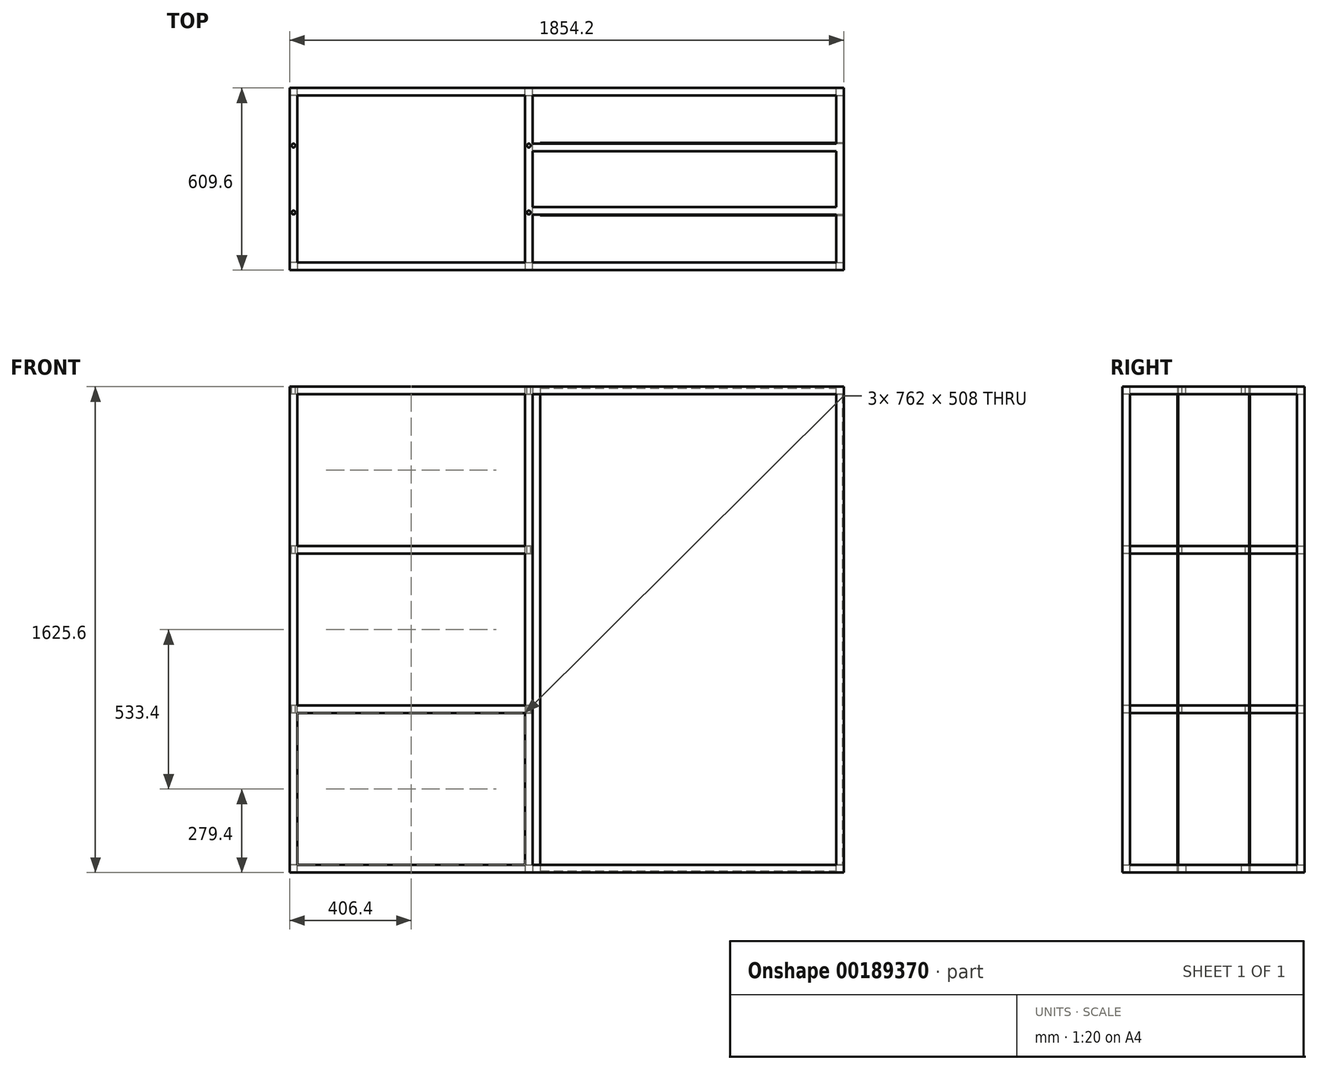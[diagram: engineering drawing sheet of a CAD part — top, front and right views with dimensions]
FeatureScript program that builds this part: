
annotation { "Feature Type Name" : "Feature", "Feature Type Description" : "" }
export const myFeature = defineFeature(function(context is Context, id is Id, definition is map)
    precondition{}
    {
        {
            var Q0;
            Q0=qCreatedBy(makeId("Front.planeOp"),FACE);
            var sketch = newSketch(context, id + "F0", { "sketchPlane" : qUnion([Q0])});
            skLineSegment(sketch, "E0.bottom", {"start": v(0, 0) * mm, "end": v(25.4, 0) * mm});
            skLineSegment(sketch, "E0.top", {"start": v(0, 25.4) * mm, "end": v(25.4, 25.4) * mm});
            skLineSegment(sketch, "E0.left", {"start": v(0, 0) * mm, "end": v(0, 25.4) * mm});
            skLineSegment(sketch, "E0.right", {"start": v(25.4, 0) * mm, "end": v(25.4, 25.4) * mm});
            skLineSegment(sketch, "E1.bottom", {"start": v(0, 533.4) * mm, "end": v(25.4, 533.4) * mm});
            skLineSegment(sketch, "E1.top", {"start": v(0, 558.8) * mm, "end": v(25.4, 558.8) * mm});
            skLineSegment(sketch, "E1.left", {"start": v(0, 533.4) * mm, "end": v(0, 558.8) * mm});
            skLineSegment(sketch, "E1.right", {"start": v(25.4, 533.4) * mm, "end": v(25.4, 558.8) * mm});
            skLineSegment(sketch, "E2.bottom", {"start": v(0, 1066.8) * mm, "end": v(25.4, 1066.8) * mm});
            skLineSegment(sketch, "E2.top", {"start": v(0, 1092.2) * mm, "end": v(25.4, 1092.2) * mm});
            skLineSegment(sketch, "E2.left", {"start": v(0, 1066.8) * mm, "end": v(0, 1092.2) * mm});
            skLineSegment(sketch, "E2.right", {"start": v(25.4, 1066.8) * mm, "end": v(25.4, 1092.2) * mm});
            skLineSegment(sketch, "E3.bottom", {"start": v(0, 1600.2) * mm, "end": v(25.4, 1600.2) * mm});
            skLineSegment(sketch, "E3.top", {"start": v(0, 1625.6) * mm, "end": v(25.4, 1625.6) * mm});
            skLineSegment(sketch, "E3.left", {"start": v(0, 1600.2) * mm, "end": v(0, 1625.6) * mm});
            skLineSegment(sketch, "E3.right", {"start": v(25.4, 1600.2) * mm, "end": v(25.4, 1625.6) * mm});
            skLineSegment(sketch, "E4", {"start": v(0, 25.4) * mm, "end": v(0, 558.8) * mm, "construction": true});
            skLineSegment(sketch, "E5", {"start": v(0, 558.8) * mm, "end": v(0, 1092.2) * mm, "construction": true});
            skLineSegment(sketch, "E6", {"start": v(0, 1092.2) * mm, "end": v(0, 1625.6) * mm, "construction": true});
            skLineSegment(sketch, "E7.bottom", {"start": v(787.4, 1625.6) * mm, "end": v(812.8, 1625.6) * mm});
            skLineSegment(sketch, "E7.top", {"start": v(787.4, 1600.2) * mm, "end": v(812.8, 1600.2) * mm});
            skLineSegment(sketch, "E7.left", {"start": v(787.4, 1625.6) * mm, "end": v(787.4, 1600.2) * mm});
            skLineSegment(sketch, "E7.right", {"start": v(812.8, 1625.6) * mm, "end": v(812.8, 1600.2) * mm});
            skLineSegment(sketch, "E8.bottom", {"start": v(787.4, 1092.2) * mm, "end": v(812.8, 1092.2) * mm});
            skLineSegment(sketch, "E8.top", {"start": v(787.4, 1066.8) * mm, "end": v(812.8, 1066.8) * mm});
            skLineSegment(sketch, "E8.left", {"start": v(787.4, 1092.2) * mm, "end": v(787.4, 1066.8) * mm});
            skLineSegment(sketch, "E8.right", {"start": v(812.8, 1092.2) * mm, "end": v(812.8, 1066.8) * mm});
            skLineSegment(sketch, "E9.bottom", {"start": v(787.4, 558.8) * mm, "end": v(812.8, 558.8) * mm});
            skLineSegment(sketch, "E9.top", {"start": v(787.4, 533.4) * mm, "end": v(812.8, 533.4) * mm});
            skLineSegment(sketch, "E9.left", {"start": v(787.4, 558.8) * mm, "end": v(787.4, 533.4) * mm});
            skLineSegment(sketch, "E9.right", {"start": v(812.8, 558.8) * mm, "end": v(812.8, 533.4) * mm});
            skLineSegment(sketch, "E10.bottom", {"start": v(787.4, 25.4) * mm, "end": v(812.8, 25.4) * mm});
            skLineSegment(sketch, "E10.top", {"start": v(787.4, 0) * mm, "end": v(812.8, 0) * mm});
            skLineSegment(sketch, "E10.left", {"start": v(787.4, 25.4) * mm, "end": v(787.4, 0) * mm});
            skLineSegment(sketch, "E10.right", {"start": v(812.8, 25.4) * mm, "end": v(812.8, 0) * mm});
            skLineSegment(sketch, "E11.bottom", {"start": v(1854.2, 1625.6) * mm, "end": v(1828.8, 1625.6) * mm});
            skLineSegment(sketch, "E11.top", {"start": v(1854.2, 1600.2) * mm, "end": v(1828.8, 1600.2) * mm});
            skLineSegment(sketch, "E11.left", {"start": v(1854.2, 1625.6) * mm, "end": v(1854.2, 1600.2) * mm});
            skLineSegment(sketch, "E11.right", {"start": v(1828.8, 1625.6) * mm, "end": v(1828.8, 1600.2) * mm});
            skLineSegment(sketch, "E12.bottom", {"start": v(1854.2, 0) * mm, "end": v(1828.8, 0) * mm});
            skLineSegment(sketch, "E12.top", {"start": v(1854.2, 25.4) * mm, "end": v(1828.8, 25.4) * mm});
            skLineSegment(sketch, "E12.left", {"start": v(1854.2, 0) * mm, "end": v(1854.2, 25.4) * mm});
            skLineSegment(sketch, "E12.right", {"start": v(1828.8, 0) * mm, "end": v(1828.8, 25.4) * mm});
            skSolve(sketch);
        }
        {
            var Q0;
            Q0 = qSketchRegion(id + "F0", true);
            extrude(context, id + "F1", {"entities" : qUnion([Q0]), "depth" : 609.6 * mm});
        }
        {
            var Q0;
            Q0=qCreatedBy(makeId("Right.planeOp"),FACE);
            var sketch = newSketch(context, id + "F2", { "sketchPlane" : qUnion([Q0])});
            skLineSegment(sketch, "E13.bottom", {"start": v(-609.6, 1600.2) * mm, "end": v(-584.2, 1600.2) * mm});
            skLineSegment(sketch, "E13.top", {"start": v(-609.6, 1625.6) * mm, "end": v(-584.2, 1625.6) * mm});
            skLineSegment(sketch, "E13.left", {"start": v(-609.6, 1625.6) * mm, "end": v(-609.6, 1600.2) * mm});
            skLineSegment(sketch, "E13.right", {"start": v(-584.2, 1625.6) * mm, "end": v(-584.2, 1600.2) * mm});
            skLineSegment(sketch, "E14.bottom", {"start": v(0, 1600.2) * mm, "end": v(-25.4, 1600.2) * mm});
            skLineSegment(sketch, "E14.top", {"start": v(0, 1625.6) * mm, "end": v(-25.4, 1625.6) * mm});
            skLineSegment(sketch, "E14.left", {"start": v(-25.4, 1625.6) * mm, "end": v(-25.4, 1600.2) * mm});
            skLineSegment(sketch, "E14.right", {"start": v(0, 1625.6) * mm, "end": v(0, 1600.2) * mm});
            skLineSegment(sketch, "E15.bottom", {"start": v(-609.6, 0) * mm, "end": v(-584.2, 0) * mm});
            skLineSegment(sketch, "E15.top", {"start": v(-609.6, 25.4) * mm, "end": v(-584.2, 25.4) * mm});
            skLineSegment(sketch, "E15.left", {"start": v(-609.6, 0) * mm, "end": v(-609.6, 25.4) * mm});
            skLineSegment(sketch, "E15.right", {"start": v(-584.2, 0) * mm, "end": v(-584.2, 25.4) * mm});
            skLineSegment(sketch, "E16.bottom", {"start": v(0, 0) * mm, "end": v(-25.4, 0) * mm});
            skLineSegment(sketch, "E16.top", {"start": v(0, 25.4) * mm, "end": v(-25.4, 25.4) * mm});
            skLineSegment(sketch, "E16.left", {"start": v(-25.4, 0) * mm, "end": v(-25.4, 25.4) * mm});
            skLineSegment(sketch, "E16.right", {"start": v(0, 0) * mm, "end": v(0, 25.4) * mm});
            skSolve(sketch);
        }
        {
            var Q0;
            Q0 = qSketchRegion(id + "F2", true);
            var Q1;
            Q1=makeQuery(id+"F1.opExtrude","SWEPT_FACE",FACE,{"disambiguationData":[OSD([sQuery(id+"F0.wireOp",EDGE,"E11.left")])]});
            extrude(context, id + "F3", {"entities" : qUnion([Q0]), "operationType" : NewBodyOperationType.ADD, "endBound" : BoundingType.UP_TO_SURFACE, "endBoundEntityFace" : qUnion([Q1]), "depth" : 25.4 * mm});
        }
        {
            var Q0;
            Q0=qCreatedBy(makeId("Right.planeOp"),FACE);
            var sketch = newSketch(context, id + "F4", { "sketchPlane" : qUnion([Q0])});
            skLineSegment(sketch, "E17.bottom", {"start": v(-609.6, 533.4) * mm, "end": v(-584.2, 533.4) * mm});
            skLineSegment(sketch, "E17.top", {"start": v(-609.6, 558.8) * mm, "end": v(-584.2, 558.8) * mm});
            skLineSegment(sketch, "E17.left", {"start": v(-609.6, 533.4) * mm, "end": v(-609.6, 558.8) * mm});
            skLineSegment(sketch, "E17.right", {"start": v(-584.2, 533.4) * mm, "end": v(-584.2, 558.8) * mm});
            skLineSegment(sketch, "E18.bottom", {"start": v(0, 533.4) * mm, "end": v(-25.4, 533.4) * mm});
            skLineSegment(sketch, "E18.top", {"start": v(0, 558.8) * mm, "end": v(-25.4, 558.8) * mm});
            skLineSegment(sketch, "E18.left", {"start": v(0, 533.4) * mm, "end": v(0, 558.8) * mm});
            skLineSegment(sketch, "E18.right", {"start": v(-25.4, 533.4) * mm, "end": v(-25.4, 558.8) * mm});
            skLineSegment(sketch, "E19.bottom", {"start": v(-609.6, 1092.2) * mm, "end": v(-584.2, 1092.2) * mm});
            skLineSegment(sketch, "E19.top", {"start": v(-609.6, 1066.8) * mm, "end": v(-584.2, 1066.8) * mm});
            skLineSegment(sketch, "E19.left", {"start": v(-609.6, 1092.2) * mm, "end": v(-609.6, 1066.8) * mm});
            skLineSegment(sketch, "E19.right", {"start": v(-584.2, 1092.2) * mm, "end": v(-584.2, 1066.8) * mm});
            skLineSegment(sketch, "E20.bottom", {"start": v(0, 1092.2) * mm, "end": v(-25.4, 1092.2) * mm});
            skLineSegment(sketch, "E20.top", {"start": v(0, 1066.8) * mm, "end": v(-25.4, 1066.8) * mm});
            skLineSegment(sketch, "E20.left", {"start": v(0, 1092.2) * mm, "end": v(0, 1066.8) * mm});
            skLineSegment(sketch, "E20.right", {"start": v(-25.4, 1092.2) * mm, "end": v(-25.4, 1066.8) * mm});
            skSolve(sketch);
        }
        {
            var Q0;
            Q0 = qSketchRegion(id + "F4", true);
            var Q1;
            Q1=makeQuery(id+"F1.opExtrude","SWEPT_FACE",FACE,{"disambiguationData":[OSD([sQuery(id+"F0.wireOp",EDGE,"E8.right")])]});
            extrude(context, id + "F5", {"entities" : qUnion([Q0]), "operationType" : NewBodyOperationType.ADD, "endBound" : BoundingType.UP_TO_SURFACE, "endBoundEntityFace" : qUnion([Q1]), "depth" : 25.4 * mm});
        }
        {
            var Q0;
            Q0=qCreatedBy(makeId("Top.planeOp"),FACE);
            var sketch = newSketch(context, id + "F6", { "sketchPlane" : qUnion([Q0])});
            skLineSegment(sketch, "E21.bottom", {"start": v(0, 0) * mm, "end": v(25.4, 0) * mm});
            skLineSegment(sketch, "E21.top", {"start": v(0, -25.4) * mm, "end": v(25.4, -25.4) * mm});
            skLineSegment(sketch, "E21.left", {"start": v(0, 0) * mm, "end": v(0, -25.4) * mm});
            skLineSegment(sketch, "E21.right", {"start": v(25.4, 0) * mm, "end": v(25.4, -25.4) * mm});
            skLineSegment(sketch, "E22.bottom", {"start": v(812.8, 0) * mm, "end": v(787.4, 0) * mm});
            skLineSegment(sketch, "E22.top", {"start": v(812.8, -25.4) * mm, "end": v(787.4, -25.4) * mm});
            skLineSegment(sketch, "E22.left", {"start": v(812.8, 0) * mm, "end": v(812.8, -25.4) * mm});
            skLineSegment(sketch, "E22.right", {"start": v(787.4, 0) * mm, "end": v(787.4, -25.4) * mm});
            skLineSegment(sketch, "E23.bottom", {"start": v(0, -609.6) * mm, "end": v(25.4, -609.6) * mm});
            skLineSegment(sketch, "E23.top", {"start": v(0, -584.2) * mm, "end": v(25.4, -584.2) * mm});
            skLineSegment(sketch, "E23.left", {"start": v(0, -609.6) * mm, "end": v(0, -584.2) * mm});
            skLineSegment(sketch, "E23.right", {"start": v(25.4, -609.6) * mm, "end": v(25.4, -584.2) * mm});
            skLineSegment(sketch, "E24.bottom", {"start": v(812.8, -609.6) * mm, "end": v(787.4, -609.6) * mm});
            skLineSegment(sketch, "E24.top", {"start": v(812.8, -584.2) * mm, "end": v(787.4, -584.2) * mm});
            skLineSegment(sketch, "E24.left", {"start": v(812.8, -609.6) * mm, "end": v(812.8, -584.2) * mm});
            skLineSegment(sketch, "E24.right", {"start": v(787.4, -609.6) * mm, "end": v(787.4, -584.2) * mm});
            skPoint(sketch, "E25.firstSnap0", {"position": v(800.1, -584.2) * mm});
            skLineSegment(sketch, "E25.bottom", {"start": v(1854.2, -584.2) * mm, "end": v(1828.8, -584.2) * mm});
            skLineSegment(sketch, "E25.top", {"start": v(1854.2, -609.6) * mm, "end": v(1828.8, -609.6) * mm});
            skLineSegment(sketch, "E25.left", {"start": v(1854.2, -584.2) * mm, "end": v(1854.2, -609.6) * mm});
            skLineSegment(sketch, "E25.right", {"start": v(1828.8, -584.2) * mm, "end": v(1828.8, -609.6) * mm});
            skLineSegment(sketch, "E26.bottom", {"start": v(1854.2, 0) * mm, "end": v(1828.8, 0) * mm});
            skLineSegment(sketch, "E26.top", {"start": v(1854.2, -25.4) * mm, "end": v(1828.8, -25.4) * mm});
            skLineSegment(sketch, "E26.left", {"start": v(1854.2, 0) * mm, "end": v(1854.2, -25.4) * mm});
            skLineSegment(sketch, "E26.right", {"start": v(1828.8, 0) * mm, "end": v(1828.8, -25.4) * mm});
            skSolve(sketch);
        }
        {
            var Q0;
            Q0 = qSketchRegion(id + "F6", true);
            var Q1;
            Q1=makeQuery(id+"F3.boolean.opBoolean","MERGE",FACE,{"derivedFrom":[makeQuery(id+"F1.opExtrude","SWEPT_FACE",FACE,{"disambiguationData":[OSD([sQuery(id+"F0.wireOp",EDGE,"E3.top")])]}),makeQuery(id+"F1.opExtrude","SWEPT_FACE",FACE,{"disambiguationData":[OSD([sQuery(id+"F0.wireOp",EDGE,"E7.bottom")])]}),makeQuery(id+"F1.opExtrude","SWEPT_FACE",FACE,{"disambiguationData":[OSD([sQuery(id+"F0.wireOp",EDGE,"E11.bottom")])]}),makeQuery(id+"F3.opExtrude","SWEPT_FACE",FACE,{"disambiguationData":[OSD([sQuery(id+"F2.wireOp",EDGE,"E13.top")])]}),makeQuery(id+"F3.opExtrude","SWEPT_FACE",FACE,{"disambiguationData":[OSD([sQuery(id+"F2.wireOp",EDGE,"E14.top")])]})]});
            extrude(context, id + "F7", {"entities" : qUnion([Q0]), "operationType" : NewBodyOperationType.ADD, "endBound" : BoundingType.UP_TO_SURFACE, "endBoundEntityFace" : qUnion([Q1]), "depth" : 25.4 * mm});
        }
        {
            var Q0;
            Q0=makeQuery(id+"F1.opExtrude","SWEPT_FACE",FACE,{"disambiguationData":[OSD([sQuery(id+"F0.wireOp",EDGE,"E7.right")])]});
            var sketch = newSketch(context, id + "F8", { "sketchPlane" : qUnion([Q0])});
            skLineSegment(sketch, "E27.bottom", {"start": v(-423.33, 1625.6) * mm, "end": v(-397.93, 1625.6) * mm});
            skLineSegment(sketch, "E27.top", {"start": v(-423.33, 1600.2) * mm, "end": v(-397.93, 1600.2) * mm});
            skLineSegment(sketch, "E27.left", {"start": v(-423.33, 1625.6) * mm, "end": v(-423.33, 1600.2) * mm});
            skLineSegment(sketch, "E27.right", {"start": v(-397.93, 1625.6) * mm, "end": v(-397.93, 1600.2) * mm});
            skLineSegment(sketch, "E28.bottom", {"start": v(-186.27, 1625.6) * mm, "end": v(-211.67, 1625.6) * mm});
            skLineSegment(sketch, "E28.top", {"start": v(-186.27, 1600.2) * mm, "end": v(-211.67, 1600.2) * mm});
            skLineSegment(sketch, "E28.left", {"start": v(-186.27, 1625.6) * mm, "end": v(-186.27, 1600.2) * mm});
            skLineSegment(sketch, "E28.right", {"start": v(-211.67, 1625.6) * mm, "end": v(-211.67, 1600.2) * mm});
            skLineSegment(sketch, "E29.bottom", {"start": v(-423.33, 25.4) * mm, "end": v(-397.93, 25.4) * mm});
            skLineSegment(sketch, "E29.top", {"start": v(-423.33, 0) * mm, "end": v(-397.93, 0) * mm});
            skLineSegment(sketch, "E29.left", {"start": v(-423.33, 25.4) * mm, "end": v(-423.33, 0) * mm});
            skLineSegment(sketch, "E29.right", {"start": v(-397.93, 25.4) * mm, "end": v(-397.93, 0) * mm});
            skLineSegment(sketch, "E30.bottom", {"start": v(-186.27, 0) * mm, "end": v(-211.67, 0) * mm});
            skLineSegment(sketch, "E30.top", {"start": v(-186.27, 25.4) * mm, "end": v(-211.67, 25.4) * mm});
            skLineSegment(sketch, "E30.left", {"start": v(-186.27, 0) * mm, "end": v(-186.27, 25.4) * mm});
            skLineSegment(sketch, "E30.right", {"start": v(-211.67, 0) * mm, "end": v(-211.67, 25.4) * mm});
            skLineSegment(sketch, "E31", {"start": v(-609.6, 1625.6) * mm, "end": v(-423.33, 1625.6) * mm, "construction": true});
            skLineSegment(sketch, "E32", {"start": v(-397.93, 1625.6) * mm, "end": v(-211.67, 1625.6) * mm, "construction": true});
            skLineSegment(sketch, "E33", {"start": v(-186.27, 1625.6) * mm, "end": v(0, 1625.6) * mm, "construction": true});
            skSolve(sketch);
        }
        {
            var Q0;
            Q0 = qSketchRegion(id + "F8", true);
            var Q1;
            Q1=makeQuery(id+"F7.boolean.opBoolean","MERGE",FACE,{"derivedFrom":[makeQuery(id+"F1.opExtrude","SWEPT_FACE",FACE,{"disambiguationData":[OSD([sQuery(id+"F0.wireOp",EDGE,"E11.left")])]}),makeQuery(id+"F1.opExtrude","SWEPT_FACE",FACE,{"disambiguationData":[OSD([sQuery(id+"F0.wireOp",EDGE,"E12.left")])]}),makeQuery(id+"F7.opExtrude","SWEPT_FACE",FACE,{"disambiguationData":[OSD([sQuery(id+"F6.wireOp",EDGE,"E25.left")])]}),makeQuery(id+"F7.opExtrude","SWEPT_FACE",FACE,{"disambiguationData":[OSD([sQuery(id+"F6.wireOp",EDGE,"E26.left")])]})]});
            extrude(context, id + "F9", {"entities" : qUnion([Q0]), "operationType" : NewBodyOperationType.ADD, "endBound" : BoundingType.UP_TO_SURFACE, "endBoundEntityFace" : qUnion([Q1]), "depth" : 25.4 * mm});
        }
        {
            var Q0;
            Q0=makeQuery(id+"F9.opExtrude","SWEPT_FACE",FACE,{"disambiguationData":[OSD([sQuery(id+"F8.wireOp",EDGE,"E27.left")])]});
            var sketch = newSketch(context, id + "F10", { "sketchPlane" : qUnion([Q0])});
            skLineSegment(sketch, "E34.bottom", {"start": v(838.2, 1620.52) * mm, "end": v(1849.12, 1620.52) * mm});
            skLineSegment(sketch, "E34.top", {"start": v(838.2, 5.08) * mm, "end": v(1849.12, 5.08) * mm});
            skLineSegment(sketch, "E34.left", {"start": v(838.2, 1620.52) * mm, "end": v(838.2, 5.08) * mm});
            skLineSegment(sketch, "E34.right", {"start": v(1849.12, 1620.52) * mm, "end": v(1849.12, 5.08) * mm});
            skSolve(sketch);
        }
        {
            var Q0;
            Q0 = qSketchRegion(id + "F10", true);
            extrude(context, id + "F11", {"entities" : qUnion([Q0]), "operationType" : NewBodyOperationType.ADD, "depth" : 3.05 * mm});
        }
        {
            var Q0;
            Q0=makeQuery(id+"F9.opExtrude","SWEPT_FACE",FACE,{"disambiguationData":[OSD([sQuery(id+"F8.wireOp",EDGE,"E28.left")])]});
            var sketch = newSketch(context, id + "F12", { "sketchPlane" : qUnion([Q0])});
            skLineSegment(sketch, "E35.0", {"start": v(-838.2, 1620.52) * mm, "end": v(-1849.12, 1620.52) * mm});
            skLineSegment(sketch, "E35.1", {"start": v(-838.2, 5.08) * mm, "end": v(-1849.12, 5.08) * mm});
            skLineSegment(sketch, "E35.2", {"start": v(-838.2, 1620.52) * mm, "end": v(-838.2, 5.08) * mm});
            skLineSegment(sketch, "E35.3", {"start": v(-1849.12, 1620.52) * mm, "end": v(-1849.12, 5.08) * mm});
            skSolve(sketch);
        }
        {
            var Q0;
            Q0 = qSketchRegion(id + "F12", true);
            extrude(context, id + "F13", {"entities" : qUnion([Q0]), "operationType" : NewBodyOperationType.ADD, "depth" : 3.05 * mm});
        }
        {
            var Q0;
            Q0=makeQuery(id+"F9.boolean.opBoolean","MERGE",FACE,{"derivedFrom":[makeQuery(id+"F3.boolean.opBoolean","MERGE",FACE,{"derivedFrom":[makeQuery(id+"F1.opExtrude","SWEPT_FACE",FACE,{"disambiguationData":[OSD([sQuery(id+"F0.wireOp",EDGE,"E3.top")])]}),makeQuery(id+"F1.opExtrude","SWEPT_FACE",FACE,{"disambiguationData":[OSD([sQuery(id+"F0.wireOp",EDGE,"E7.bottom")])]}),makeQuery(id+"F1.opExtrude","SWEPT_FACE",FACE,{"disambiguationData":[OSD([sQuery(id+"F0.wireOp",EDGE,"E11.bottom")])]}),makeQuery(id+"F3.opExtrude","SWEPT_FACE",FACE,{"disambiguationData":[OSD([sQuery(id+"F2.wireOp",EDGE,"E13.top")])]}),makeQuery(id+"F3.opExtrude","SWEPT_FACE",FACE,{"disambiguationData":[OSD([sQuery(id+"F2.wireOp",EDGE,"E14.top")])]})]}),makeQuery(id+"F9.opExtrude","SWEPT_FACE",FACE,{"disambiguationData":[OSD([sQuery(id+"F8.wireOp",EDGE,"E27.bottom")])]}),makeQuery(id+"F9.opExtrude","SWEPT_FACE",FACE,{"disambiguationData":[OSD([sQuery(id+"F8.wireOp",EDGE,"E28.bottom")])]})]});
            var sketch = newSketch(context, id + "F14", { "sketchPlane" : qUnion([Q0])});
            skLineSegment(sketch, "E36.bottom", {"start": v(800.1, -416.81) * mm, "end": v(12.7, -416.81) * mm, "construction": true});
            skLineSegment(sketch, "E36.top", {"start": v(800.1, -192.79) * mm, "end": v(12.7, -192.79) * mm, "construction": true});
            skLineSegment(sketch, "E36.left", {"start": v(800.1, -416.81) * mm, "end": v(800.1, -192.79) * mm, "construction": true});
            skLineSegment(sketch, "E36.right", {"start": v(12.7, -416.81) * mm, "end": v(12.7, -192.79) * mm, "construction": true});
            skLineSegment(sketch, "E37", {"start": v(12.7, -192.79) * mm, "end": v(12.7, 0) * mm, "construction": true});
            skLineSegment(sketch, "E38", {"start": v(12.7, -416.81) * mm, "end": v(12.7, -609.6) * mm, "construction": true});
            skCircle(sketch, "E39", {"center": v(12.7, -416.81) * mm, "radius": 6.35 * mm});
            skCircle(sketch, "E40", {"center": v(800.1, -416.81) * mm, "radius": 6.35 * mm});
            skCircle(sketch, "E41", {"center": v(800.1, -192.79) * mm, "radius": 6.35 * mm});
            skCircle(sketch, "E42", {"center": v(12.7, -192.79) * mm, "radius": 6.35 * mm});
            skSolve(sketch);
        }
        {
            var Q0;
            Q0 = qSketchRegion(id + "F14", true);
            var Q1;
            {var subQ0=makeQuery(id+"F3.opExtrude","SWEPT_FACE",FACE,{"disambiguationData":[OSD([sQuery(id+"F2.wireOp",EDGE,"E15.top")])]});var subQ1=makeQuery(id+"F1.opExtrude","SWEPT_FACE",FACE,{"disambiguationData":[OSD([sQuery(id+"F0.wireOp",EDGE,"E10.bottom")])]});var subQ2=makeQuery(id+"F1.opExtrude","SWEPT_FACE",FACE,{"disambiguationData":[OSD([sQuery(id+"F0.wireOp",EDGE,"E12.top")])]});var subQ3=makeQuery(id+"F1.opExtrude","SWEPT_FACE",FACE,{"disambiguationData":[OSD([sQuery(id+"F0.wireOp",EDGE,"E0.top")])]});var subQ4=makeQuery(id+"F3.opExtrude","SWEPT_FACE",FACE,{"disambiguationData":[OSD([sQuery(id+"F2.wireOp",EDGE,"E16.top")])]});Q1=makeQuery(id+"F7.boolean.opBoolean","SPLIT",FACE,{"disambiguationData":[TD([subQ3,makeQuery(id+"F1.opExtrude","SWEPT_FACE",FACE,{"disambiguationData":[OSD([sQuery(id+"F0.wireOp",EDGE,"E0.left")])]}),makeQuery(id+"F1.opExtrude","SWEPT_FACE",FACE,{"disambiguationData":[OSD([sQuery(id+"F0.wireOp",EDGE,"E0.right")])]}),makeQuery(id+"F1.opExtrude","SWEPT_FACE",FACE,{"disambiguationData":[OSD([sQuery(id+"F0.wireOp",EDGE,"E1.left")])]}),makeQuery(id+"F1.opExtrude","SWEPT_FACE",FACE,{"disambiguationData":[OSD([sQuery(id+"F0.wireOp",EDGE,"E2.left")])]}),makeQuery(id+"F1.opExtrude","SWEPT_FACE",FACE,{"disambiguationData":[OSD([sQuery(id+"F0.wireOp",EDGE,"E3.left")])]}),subQ1,subQ2,subQ0,makeQuery(id+"F3.opExtrude","SWEPT_FACE",FACE,{"disambiguationData":[OSD([sQuery(id+"F2.wireOp",EDGE,"E15.right")])]}),subQ4,makeQuery(id+"F3.opExtrude","SWEPT_FACE",FACE,{"disambiguationData":[OSD([sQuery(id+"F2.wireOp",EDGE,"E16.left")])]}),makeQuery(id+"F7.opExtrude","SWEPT_FACE",FACE,{"disambiguationData":[OSD([sQuery(id+"F6.wireOp",EDGE,"E21.top")])]}),makeQuery(id+"F7.opExtrude","SWEPT_FACE",FACE,{"disambiguationData":[OSD([sQuery(id+"F6.wireOp",EDGE,"E21.left")])]}),makeQuery(id+"F7.opExtrude","SWEPT_FACE",FACE,{"disambiguationData":[OSD([sQuery(id+"F6.wireOp",EDGE,"E21.right")])]}),makeQuery(id+"F7.opExtrude","SWEPT_FACE",FACE,{"disambiguationData":[OSD([sQuery(id+"F6.wireOp",EDGE,"E23.top")])]}),makeQuery(id+"F7.opExtrude","SWEPT_FACE",FACE,{"disambiguationData":[OSD([sQuery(id+"F6.wireOp",EDGE,"E23.left")])]}),makeQuery(id+"F7.opExtrude","SWEPT_FACE",FACE,{"disambiguationData":[OSD([sQuery(id+"F6.wireOp",EDGE,"E23.right")])]})])],"derivedFrom":makeQuery(id+"F3.boolean.opBoolean","MERGE",FACE,{"derivedFrom":[subQ3,subQ1,subQ2,subQ0,subQ4]})});}
            extrude(context, id + "F15", {"entities" : qUnion([Q0]), "operationType" : NewBodyOperationType.REMOVE, "endBound" : BoundingType.UP_TO_SURFACE, "oppositeDirection" : true, "endBoundEntityFace" : qUnion([Q1]), "depth" : 25.4 * mm});
        }
    });
